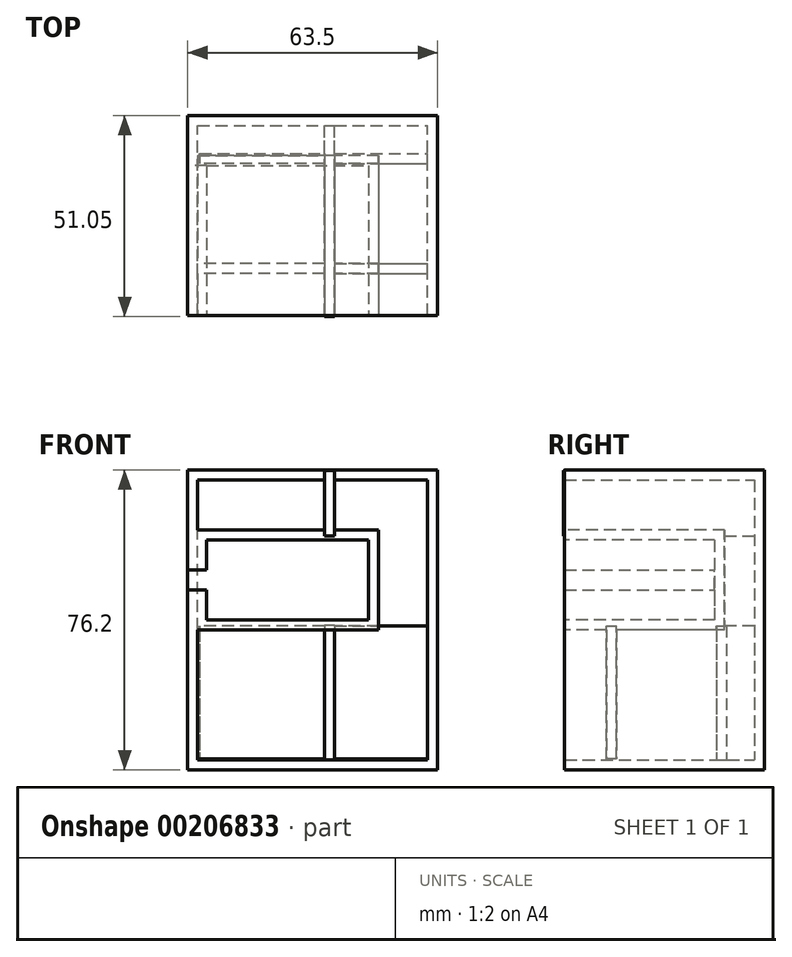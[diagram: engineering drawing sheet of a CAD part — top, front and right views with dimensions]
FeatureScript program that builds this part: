
annotation { "Feature Type Name" : "Feature", "Feature Type Description" : "" }
export const myFeature = defineFeature(function(context is Context, id is Id, definition is map)
    precondition{}
    {
        {
            var Q0;
            Q0=qCreatedBy(makeId("Top.planeOp"),FACE);
            var sketch = newSketch(context, id + "F0", { "sketchPlane" : qUnion([Q0])});
            skLineSegment(sketch, "E0.bottom", {"start": v(-36.02, -39.87) * mm, "end": v(27.48, -39.87) * mm});
            skLineSegment(sketch, "E0.top", {"start": v(-36.02, 10.93) * mm, "end": v(27.48, 10.93) * mm});
            skLineSegment(sketch, "E0.left", {"start": v(-36.02, -39.87) * mm, "end": v(-36.02, 10.93) * mm});
            skLineSegment(sketch, "E0.right", {"start": v(27.48, -39.87) * mm, "end": v(27.48, 10.93) * mm});
            skSolve(sketch);
        }
        {
            var Q0;
            Q0 = qSketchRegion(id + "F0", true);
            extrude(context, id + "F1", {"entities" : qUnion([Q0]), "depth" : 76.2 * mm});
        }
        {
            var Q0;
            Q0=makeQuery(id+"F1.opExtrude","SWEPT_FACE",FACE,{"disambiguationData":[OSD([sQuery(id+"F0.wireOp",EDGE,"E0.bottom")])]});
            var sketch = newSketch(context, id + "F2", { "sketchPlane" : qUnion([Q0])});
            skLineSegment(sketch, "E1.bottom", {"start": v(-31.2, 58.42) * mm, "end": v(9.95, 58.42) * mm});
            skLineSegment(sketch, "E1.top", {"start": v(-31.2, 38.1) * mm, "end": v(9.95, 38.1) * mm});
            skLineSegment(sketch, "E1.left", {"start": v(-31.2, 58.42) * mm, "end": v(-31.2, 50.8) * mm});
            skLineSegment(sketch, "E1.right", {"start": v(9.95, 58.42) * mm, "end": v(9.95, 38.1) * mm});
            skLineSegment(sketch, "E2.bottom", {"start": v(-31.2, 50.8) * mm, "end": v(-39.87, 50.8) * mm});
            skLineSegment(sketch, "E2.top", {"start": v(-31.2, 45.72) * mm, "end": v(-39.87, 45.72) * mm});
            skLineSegment(sketch, "E2.right", {"start": v(-39.87, 50.8) * mm, "end": v(-39.87, 45.72) * mm});
            skLineSegment(sketch, "E3.trimOffspring", {"start": v(-31.2, 45.72) * mm, "end": v(-31.2, 38.1) * mm});
            skSolve(sketch);
        }
        {
            var Q0;
            Q0 = qSketchRegion(id + "F2", true);
            extrude(context, id + "F3", {"entities" : qUnion([Q0]), "operationType" : NewBodyOperationType.REMOVE, "oppositeDirection" : true, "depth" : 38.1 * mm});
        }
        {
            var Q0;
            Q0=makeQuery(id+"F1.opExtrude","SWEPT_FACE",FACE,{"disambiguationData":[OSD([sQuery(id+"F0.wireOp",EDGE,"E0.bottom")])]});
            shell(context, id + "F4", {"entities" : qUnion([Q0]), "thickness" : 2.54 * mm});
        }
        {
            var Q0;
            Q0=qCreatedBy(makeId("Right.planeOp"),FACE);
            var sketch = newSketch(context, id + "F5", { "sketchPlane" : qUnion([Q0])});
            skLineSegment(sketch, "E4.bottom", {"start": v(-39.78, 36.7) * mm, "end": v(9.72, 36.7) * mm});
            skLineSegment(sketch, "E4.top", {"start": v(-39.78, 0) * mm, "end": v(9.72, 0) * mm});
            skLineSegment(sketch, "E4.left", {"start": v(-39.78, 36.7) * mm, "end": v(-39.78, 0) * mm});
            skLineSegment(sketch, "E4.right", {"start": v(9.72, 36.7) * mm, "end": v(9.72, 0) * mm});
            skLineSegment(sketch, "E5.bottom", {"start": v(-40.12, 59.42) * mm, "end": v(9.5, 59.42) * mm});
            skLineSegment(sketch, "E5.top", {"start": v(-40.12, 76.05) * mm, "end": v(9.5, 76.05) * mm});
            skLineSegment(sketch, "E5.left", {"start": v(-40.12, 59.42) * mm, "end": v(-40.12, 76.05) * mm});
            skLineSegment(sketch, "E5.right", {"start": v(9.5, 59.42) * mm, "end": v(9.5, 76.05) * mm});
            skSolve(sketch);
        }
        {
            var Q0;
            Q0 = qSketchRegion(id + "F5", true);
            extrude(context, id + "F6", {"entities" : qUnion([Q0]), "operationType" : NewBodyOperationType.ADD, "endBound" : BoundingType.SYMMETRIC, "depth" : 2.54 * mm});
        }
        {
            var Q0;
            Q0=qCreatedBy(makeId("Front.planeOp"),FACE);
            var sketch = newSketch(context, id + "F7", { "sketchPlane" : qUnion([Q0])});
            skLineSegment(sketch, "E6.bottom", {"start": v(-32.98, 36.61) * mm, "end": v(24.86, 36.61) * mm});
            skLineSegment(sketch, "E6.top", {"start": v(-32.98, 0) * mm, "end": v(24.86, 0) * mm});
            skLineSegment(sketch, "E6.left", {"start": v(-32.98, 36.61) * mm, "end": v(-32.98, 0) * mm});
            skLineSegment(sketch, "E6.right", {"start": v(24.86, 36.61) * mm, "end": v(24.86, 0) * mm});
            skSolve(sketch);
        }
        {
            var Q0;
            Q0 = qSketchRegion(id + "F7", true);
            extrude(context, id + "F8", {"entities" : qUnion([Q0]), "operationType" : NewBodyOperationType.ADD, "endBound" : BoundingType.SYMMETRIC, "depth" : 2.54 * mm});
        }
        {
            var Q0;
            Q0=qCreatedBy(makeId("Front.planeOp"),FACE);
            cPlane(context, id + "F9", {"entities" : qUnion([Q0]), "cplaneType" : CPlaneType.OFFSET, "offset" : 27.94 * mm, "width" : 152.4 * mm, "height" : 152.4 * mm});
        }
        {
            var Q0;
            Q0=qCreatedBy(id+"F9.planeOp",FACE);
            var sketch = newSketch(context, id + "F10", { "sketchPlane" : qUnion([Q0])});
            skLineSegment(sketch, "E7.bottom", {"start": v(-35.65, 36.6) * mm, "end": v(25.86, 36.6) * mm});
            skLineSegment(sketch, "E7.top", {"start": v(-35.65, 2.77) * mm, "end": v(25.86, 2.77) * mm});
            skLineSegment(sketch, "E7.left", {"start": v(-35.65, 36.6) * mm, "end": v(-35.65, 2.77) * mm});
            skLineSegment(sketch, "E7.right", {"start": v(25.86, 36.6) * mm, "end": v(25.86, 2.77) * mm});
            skSolve(sketch);
        }
        {
            var Q0;
            Q0 = qSketchRegion(id + "F10", true);
            extrude(context, id + "F11", {"entities" : qUnion([Q0]), "operationType" : NewBodyOperationType.ADD, "endBound" : BoundingType.SYMMETRIC, "depth" : 2.54 * mm});
        }
    });
